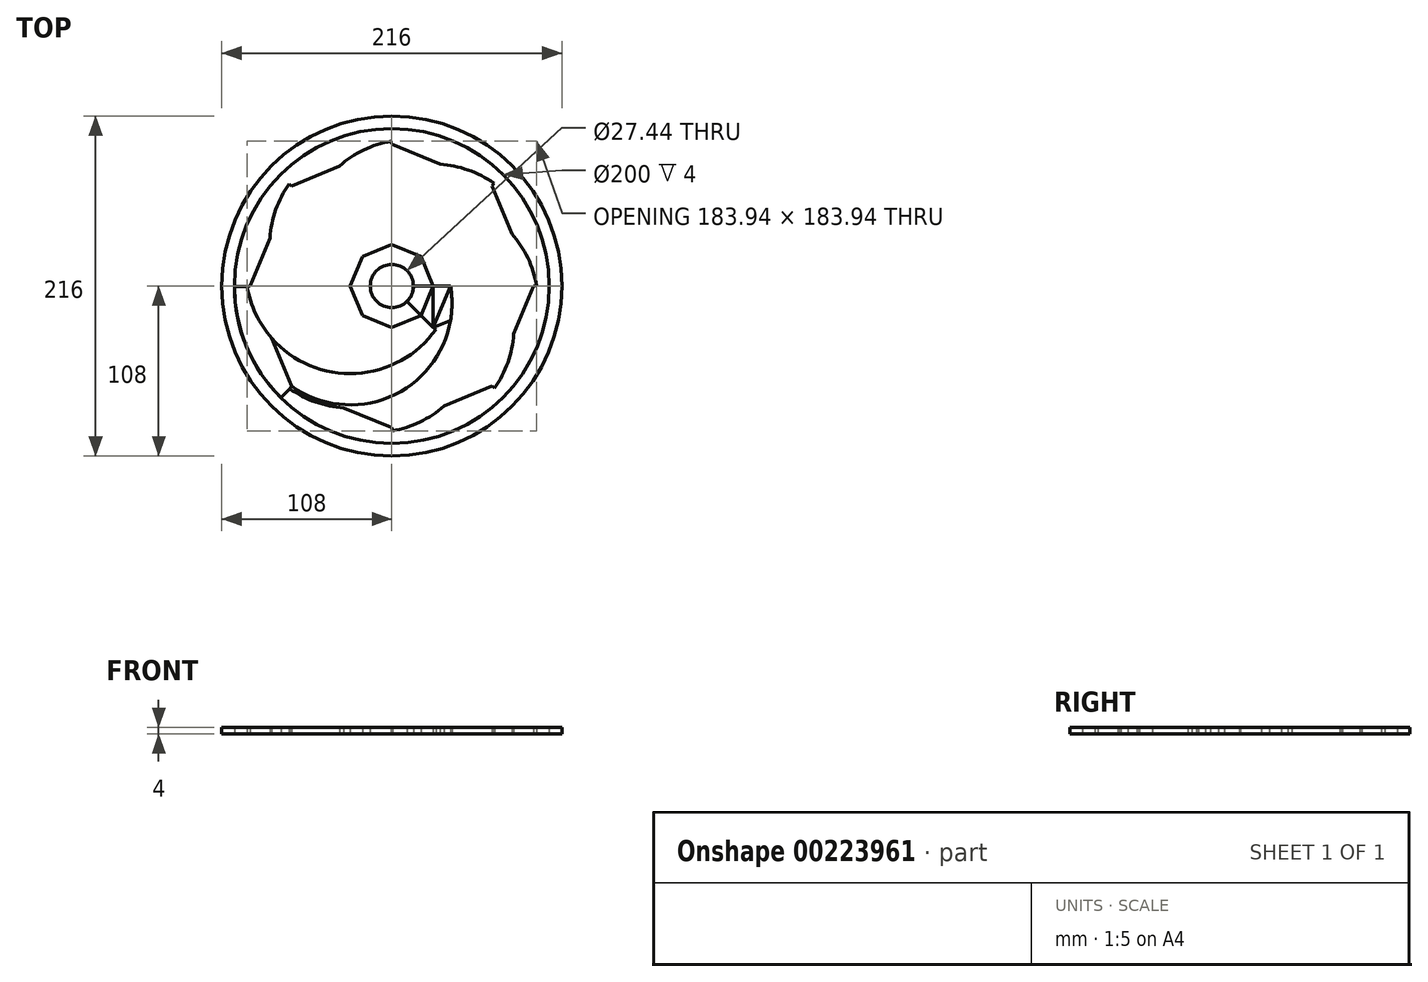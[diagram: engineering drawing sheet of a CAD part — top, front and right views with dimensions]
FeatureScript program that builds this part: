
annotation { "Feature Type Name" : "Feature", "Feature Type Description" : "" }
export const myFeature = defineFeature(function(context is Context, id is Id, definition is map)
    precondition{}
    {
        {
            assignVariable(context, id + "F0", {"name" : "t", "anyValue" : 4});
        }
        {
            var Q0;
            Q0=qCreatedBy(makeId("Top.planeOp"),FACE);
            var sketch = newSketch(context, id + "F1", { "sketchPlane" : qUnion([Q0])});
            skCircle(sketch, "E0", {"center": v(0, 0) * mm, "radius": 100 * mm});
            skCircle(sketch, "E1.cCircle", {"center": v(0, 0) * mm, "radius": 90 * mm, "construction": true});
            skLineSegment(sketch, "E1.0", {"start": v(90, 0) * mm, "end": v(63.64, -63.64) * mm, "construction": true});
            skLineSegment(sketch, "E1.1", {"start": v(63.64, -63.64) * mm, "end": v(0, -90) * mm, "construction": true});
            skLineSegment(sketch, "E1.4", {"start": v(-90, 0) * mm, "end": v(-63.64, 63.64) * mm, "construction": true});
            skLineSegment(sketch, "E1.5", {"start": v(-63.64, 63.64) * mm, "end": v(0, 90) * mm, "construction": true});
            skLineSegment(sketch, "E1.6", {"start": v(0, 90) * mm, "end": v(63.64, 63.64) * mm, "construction": true});
            skLineSegment(sketch, "E1.7", {"start": v(63.64, 63.64) * mm, "end": v(90, 0) * mm, "construction": true});
            skLineSegment(sketch, "E2.0", {"start": v(26.36, -26.36) * mm, "end": v(0, -37.28) * mm});
            skLineSegment(sketch, "E2.1", {"start": v(0, -37.28) * mm, "end": v(-26.36, -26.36) * mm});
            skLineSegment(sketch, "E2.2", {"start": v(-26.36, -26.36) * mm, "end": v(-37.28, 0) * mm});
            skLineSegment(sketch, "E2.3", {"start": v(-37.28, 0) * mm, "end": v(-26.36, 26.36) * mm});
            skLineSegment(sketch, "E2.4", {"start": v(-26.36, 26.36) * mm, "end": v(0, 37.28) * mm});
            skLineSegment(sketch, "E2.5", {"start": v(0, 37.28) * mm, "end": v(26.36, 26.36) * mm});
            skLineSegment(sketch, "E2.6", {"start": v(26.36, 26.36) * mm, "end": v(37.28, 0) * mm});
            skLineSegment(sketch, "E2.7", {"start": v(37.28, 0) * mm, "end": v(26.36, -26.36) * mm});
            skArc(sketch, "E3", {"start": v(-63.64, -63.64) * mm, "mid": v(8.08, -65.54) * mm, "end": v(37.28, 0) * mm});
            skArc(sketch, "E4.0", {"start": v(-64.8, -65.27) * mm, "mid": v(9.15, -67.23) * mm, "end": v(39.25, 0.34) * mm});
            skArc(sketch, "E5.1.0", {"start": v(0, -90) * mm, "mid": v(52.05, -40.63) * mm, "end": v(26.36, 26.36) * mm});
            skArc(sketch, "E5.1.1", {"start": v(0.34, -91.97) * mm, "mid": v(54, -41.07) * mm, "end": v(27.52, 28) * mm});
            skArc(sketch, "E5.2.0", {"start": v(63.64, -63.64) * mm, "mid": v(65.54, 8.08) * mm, "end": v(0, 37.28) * mm});
            skArc(sketch, "E5.2.1", {"start": v(65.27, -64.8) * mm, "mid": v(67.23, 9.15) * mm, "end": v(-0.34, 39.25) * mm});
            skArc(sketch, "E5.3.0", {"start": v(90, 0) * mm, "mid": v(40.63, 52.05) * mm, "end": v(-26.36, 26.36) * mm});
            skArc(sketch, "E5.3.1", {"start": v(91.97, 0.34) * mm, "mid": v(41.07, 54) * mm, "end": v(-28, 27.52) * mm});
            skArc(sketch, "E5.4.0", {"start": v(63.64, 63.64) * mm, "mid": v(-8.08, 65.54) * mm, "end": v(-37.28, 0) * mm});
            skArc(sketch, "E5.4.1", {"start": v(64.8, 65.27) * mm, "mid": v(-9.15, 67.23) * mm, "end": v(-39.25, -0.34) * mm});
            skArc(sketch, "E5.5.0", {"start": v(0, 90) * mm, "mid": v(-52.05, 40.63) * mm, "end": v(-26.36, -26.36) * mm});
            skArc(sketch, "E5.5.1", {"start": v(-0.34, 91.97) * mm, "mid": v(-54, 41.07) * mm, "end": v(-27.52, -28) * mm});
            skArc(sketch, "E5.6.0", {"start": v(-63.64, 63.64) * mm, "mid": v(-65.54, -8.08) * mm, "end": v(0, -37.28) * mm});
            skArc(sketch, "E5.6.1", {"start": v(-65.27, 64.8) * mm, "mid": v(-67.23, -9.15) * mm, "end": v(0.34, -39.25) * mm});
            skArc(sketch, "E5.7.0", {"start": v(-90, 0) * mm, "mid": v(-40.63, -52.05) * mm, "end": v(26.36, -26.36) * mm});
            skArc(sketch, "E5.7.1", {"start": v(-91.97, -0.34) * mm, "mid": v(-41.07, -54) * mm, "end": v(28, -27.52) * mm});
            skLineSegment(sketch, "E6", {"start": v(37.28, -21.84) * mm, "end": v(26.36, -26.36) * mm});
            skLineSegment(sketch, "E7", {"start": v(28, -27.52) * mm, "end": v(26.36, -26.36) * mm});
            skLineSegment(sketch, "E8", {"start": v(-64.8, -65.27) * mm, "end": v(-63.64, -63.64) * mm});
            skLineSegment(sketch, "E9", {"start": v(-63.64, -63.64) * mm, "end": v(-76.28, -33.12) * mm});
            skLineSegment(sketch, "E10.1.0", {"start": v(0, -90) * mm, "end": v(-30.52, -77.36) * mm});
            skLineSegment(sketch, "E10.1.1", {"start": v(0.34, -91.97) * mm, "end": v(0, -90) * mm});
            skLineSegment(sketch, "E10.1.2", {"start": v(39.25, 0.34) * mm, "end": v(37.28, 0) * mm});
            skLineSegment(sketch, "E10.2.0", {"start": v(63.64, -63.64) * mm, "end": v(33.12, -76.28) * mm});
            skLineSegment(sketch, "E10.2.1", {"start": v(65.27, -64.8) * mm, "end": v(63.64, -63.64) * mm});
            skLineSegment(sketch, "E10.2.2", {"start": v(27.52, 28) * mm, "end": v(26.36, 26.36) * mm});
            skLineSegment(sketch, "E10.3.0", {"start": v(90, 0) * mm, "end": v(77.36, -30.52) * mm});
            skLineSegment(sketch, "E10.3.1", {"start": v(91.97, 0.34) * mm, "end": v(90, 0) * mm});
            skLineSegment(sketch, "E10.3.2", {"start": v(-0.34, 39.25) * mm, "end": v(0, 37.28) * mm});
            skLineSegment(sketch, "E10.4.0", {"start": v(63.64, 63.64) * mm, "end": v(76.28, 33.12) * mm});
            skLineSegment(sketch, "E10.4.1", {"start": v(64.8, 65.27) * mm, "end": v(63.64, 63.64) * mm});
            skLineSegment(sketch, "E10.4.2", {"start": v(-28, 27.52) * mm, "end": v(-26.36, 26.36) * mm});
            skLineSegment(sketch, "E10.5.0", {"start": v(0, 90) * mm, "end": v(30.52, 77.36) * mm});
            skLineSegment(sketch, "E10.5.1", {"start": v(-0.34, 91.97) * mm, "end": v(0, 90) * mm});
            skLineSegment(sketch, "E10.5.2", {"start": v(-39.25, -0.34) * mm, "end": v(-37.28, 0) * mm});
            skLineSegment(sketch, "E10.6.0", {"start": v(-63.64, 63.64) * mm, "end": v(-33.12, 76.28) * mm});
            skLineSegment(sketch, "E10.6.1", {"start": v(-65.27, 64.8) * mm, "end": v(-63.64, 63.64) * mm});
            skLineSegment(sketch, "E10.6.2", {"start": v(-27.52, -28) * mm, "end": v(-26.36, -26.36) * mm});
            skLineSegment(sketch, "E10.7.0", {"start": v(-90, 0) * mm, "end": v(-77.36, 30.52) * mm});
            skLineSegment(sketch, "E10.7.1", {"start": v(-91.97, -0.34) * mm, "end": v(-90, 0) * mm});
            skLineSegment(sketch, "E10.7.2", {"start": v(0.34, -39.25) * mm, "end": v(0, -37.28) * mm});
            skLineSegment(sketch, "E11.1.0", {"start": v(41.8, 10.92) * mm, "end": v(37.28, 0) * mm});
            skLineSegment(sketch, "E11.2.0", {"start": v(21.84, 37.28) * mm, "end": v(26.36, 26.36) * mm});
            skLineSegment(sketch, "E11.3.0", {"start": v(-10.92, 41.8) * mm, "end": v(0, 37.28) * mm});
            skLineSegment(sketch, "E11.4.0", {"start": v(-37.28, 21.84) * mm, "end": v(-26.36, 26.36) * mm});
            skLineSegment(sketch, "E11.5.0", {"start": v(-41.8, -10.92) * mm, "end": v(-37.28, 0) * mm});
            skLineSegment(sketch, "E11.6.0", {"start": v(-21.84, -37.28) * mm, "end": v(-26.36, -26.36) * mm});
            skLineSegment(sketch, "E11.7.0", {"start": v(10.92, -41.8) * mm, "end": v(0, -37.28) * mm});
            skLineSegment(sketch, "E12", {"start": v(18.64, -18.64) * mm, "end": v(0, -26.36) * mm});
            skPoint(sketch, "E13", {"position": v(18.64, -18.64) * mm});
            skLineSegment(sketch, "E14", {"start": v(18.64, -18.64) * mm, "end": v(0, -37.28) * mm});
            skLineSegment(sketch, "E15", {"start": v(0, -26.36) * mm, "end": v(0, -37.28) * mm});
            skLineSegment(sketch, "E16.1.0", {"start": v(26.36, 0) * mm, "end": v(18.64, -18.64) * mm});
            skLineSegment(sketch, "E16.1.1", {"start": v(18.64, -18.64) * mm, "end": v(26.36, -26.36) * mm});
            skLineSegment(sketch, "E16.1.2", {"start": v(26.36, 0) * mm, "end": v(26.36, -26.36) * mm});
            skLineSegment(sketch, "E16.2.0", {"start": v(18.64, 18.64) * mm, "end": v(26.36, 0) * mm});
            skLineSegment(sketch, "E16.2.1", {"start": v(26.36, 0) * mm, "end": v(37.28, 0) * mm});
            skLineSegment(sketch, "E16.2.2", {"start": v(18.64, 18.64) * mm, "end": v(37.28, 0) * mm});
            skLineSegment(sketch, "E17.3.3.0", {"start": v(18.64, 18.64) * mm, "end": v(26.36, 26.36) * mm});
            skLineSegment(sketch, "E17.5.3.0", {"start": v(0, 26.36) * mm, "end": v(18.64, 18.64) * mm});
            skLineSegment(sketch, "E17.6.3.0", {"start": v(0, 26.36) * mm, "end": v(26.36, 26.36) * mm});
            skLineSegment(sketch, "E17.3.4.0", {"start": v(0, 26.36) * mm, "end": v(0, 37.28) * mm});
            skLineSegment(sketch, "E17.5.4.0", {"start": v(-18.64, 18.64) * mm, "end": v(0, 26.36) * mm});
            skLineSegment(sketch, "E17.6.4.0", {"start": v(-18.64, 18.64) * mm, "end": v(0, 37.28) * mm});
            skLineSegment(sketch, "E17.3.5.0", {"start": v(-18.64, 18.64) * mm, "end": v(-26.36, 26.36) * mm});
            skLineSegment(sketch, "E17.5.5.0", {"start": v(-26.36, 0) * mm, "end": v(-18.64, 18.64) * mm});
            skLineSegment(sketch, "E17.6.5.0", {"start": v(-26.36, 0) * mm, "end": v(-26.36, 26.36) * mm});
            skLineSegment(sketch, "E17.3.6.0", {"start": v(-26.36, 0) * mm, "end": v(-37.28, 0) * mm});
            skLineSegment(sketch, "E17.5.6.0", {"start": v(-18.64, -18.64) * mm, "end": v(-26.36, 0) * mm});
            skLineSegment(sketch, "E17.6.6.0", {"start": v(-18.64, -18.64) * mm, "end": v(-37.28, 0) * mm});
            skLineSegment(sketch, "E17.3.7.0", {"start": v(-18.64, -18.64) * mm, "end": v(-26.36, -26.36) * mm});
            skLineSegment(sketch, "E17.5.7.0", {"start": v(0, -26.36) * mm, "end": v(-18.64, -18.64) * mm});
            skLineSegment(sketch, "E17.6.7.0", {"start": v(0, -26.36) * mm, "end": v(-26.36, -26.36) * mm});
            skLineSegment(sketch, "E18", {"start": v(-91.97, -0.34) * mm, "end": v(-100, -0.34) * mm});
            skLineSegment(sketch, "E19.1.0", {"start": v(-64.8, -65.27) * mm, "end": v(-70.47, -70.95) * mm});
            skLineSegment(sketch, "E19.2.0", {"start": v(0.34, -91.97) * mm, "end": v(0.34, -100) * mm});
            skLineSegment(sketch, "E19.3.0", {"start": v(65.27, -64.8) * mm, "end": v(70.95, -70.47) * mm});
            skLineSegment(sketch, "E19.4.0", {"start": v(91.97, 0.34) * mm, "end": v(100, 0.34) * mm});
            skLineSegment(sketch, "E19.5.0", {"start": v(64.8, 65.27) * mm, "end": v(70.47, 70.95) * mm});
            skLineSegment(sketch, "E19.6.0", {"start": v(-0.34, 91.97) * mm, "end": v(-0.34, 100) * mm});
            skLineSegment(sketch, "E19.7.0", {"start": v(-65.27, 64.8) * mm, "end": v(-70.95, 70.47) * mm});
            skCircle(sketch, "E20", {"center": v(0, 0) * mm, "radius": 13.72 * mm});
            skLineSegment(sketch, "E21", {"start": v(0, 0) * mm, "end": v(18.64, -18.64) * mm});
            skLineSegment(sketch, "E22", {"start": v(0, 0) * mm, "end": v(26.36, 0) * mm});
            skCircle(sketch, "E23.0", {"center": v(0, 0) * mm, "radius": 108 * mm});
            skSolve(sketch);
        }
        {
            var Q0;
            Q0=makeQuery(id+"F1.imprint","IMPRINT",FACE,{"disambiguationData":[TD([[makeQuery(id+"F1.imprint","IMPRINT",EDGE,{"derivedFrom":sQuery(id+"F1.wireOp",EDGE,"E0")}),1.0]])]});
            extrude(context, id + "F2", {"entities" : qUnion([Q0]), "depth" : (getVariable(context, 't')) * mm});
        }
        {
            var Q0;
            {var subQ1=sQuery(id+"F1.wireOp",EDGE,"E6");Q0=makeQuery(id+"F1.imprint","IMPRINT",FACE,{"disambiguationData":[TD([[makeQuery(id+"F1.imprint","IMPRINT",EDGE,{"derivedFrom":subQ1}),1.0]])]});}
            extrude(context, id + "F3", {"entities" : qUnion([Q0]), "depth" : (getVariable(context, 't')) * mm});
        }
        {
            var Q0;
            {var subQ0=sQuery(id+"F1.wireOp",EDGE,"E2.7");Q0=makeQuery(id+"F1.imprint","IMPRINT",FACE,{"disambiguationData":[TD([[makeQuery(id+"F1.imprint","IMPRINT",EDGE,{"derivedFrom":subQ0}),1.0]])]});}
            extrude(context, id + "F4", {"entities" : qUnion([Q0]), "depth" : (getVariable(context, 't')) * mm});
        }
        {
            var Q0;
            Q0=makeQuery(id+"F1.imprint","IMPRINT",FACE,{"disambiguationData":[TD([[makeQuery(id+"F1.imprint","IMPRINT",EDGE,{"derivedFrom":sQuery(id+"F1.wireOp",EDGE,"E2.7")}),-1.0]])]});
            extrude(context, id + "F5", {"entities" : qUnion([Q0]), "depth" : (getVariable(context, 't')) * mm});
        }
        {
            var Q0;
            Q0=makeQuery(id+"F1.imprint","IMPRINT",FACE,{"disambiguationData":[TD([[makeQuery(id+"F1.imprint","IMPRINT",EDGE,{"derivedFrom":sQuery(id+"F1.wireOp",EDGE,"E16.1.0")}),1.0]])]});
            extrude(context, id + "F6", {"entities" : qUnion([Q0]), "depth" : (getVariable(context, 't')) * mm});
        }
        {
            var Q0;
            Q0=makeQuery(id+"F1.imprint","IMPRINT",FACE,{"disambiguationData":[TD([[makeQuery(id+"F1.imprint","IMPRINT",EDGE,{"derivedFrom":sQuery(id+"F1.wireOp",EDGE,"E12")}),-1.0]])]});
            var Q1;
            {var subQ0=sQuery(id+"F1.wireOp",EDGE,"E16.1.0");Q1=makeQuery(id+"F1.imprint","IMPRINT",FACE,{"disambiguationData":[TD([[makeQuery(id+"F1.imprint","IMPRINT",EDGE,{"derivedFrom":subQ0}),-1.0]])]});}
            extrude(context, id + "F7", {"entities" : qUnion([Q0, Q1]), "depth" : (getVariable(context, 't')) * mm});
        }
        {
            var Q0;
            Q0=makeQuery(id+"F1.imprint","IMPRINT",FACE,{"disambiguationData":[TD([[makeQuery(id+"F1.imprint","IMPRINT",EDGE,{"derivedFrom":sQuery(id+"F1.wireOp",EDGE,"E8")}),1.0]])]});
            extrude(context, id + "F8", {"entities" : qUnion([Q0]), "depth" : (getVariable(context, 't')) * mm});
        }
        {
            var Q0;
            {var subQ0=sQuery(id+"F1.wireOp",EDGE,"E16.1.0");Q0=makeQuery(id+"F1.imprint","IMPRINT",FACE,{"disambiguationData":[TD([[makeQuery(id+"F1.imprint","IMPRINT",EDGE,{"derivedFrom":subQ0}),-1.0]])]});}
            extrude(context, id + "F9", {"entities" : qUnion([Q0]), "depth" : (getVariable(context, 't')) * mm});
        }
        {
            var Q0;
            Q0 = qSketchRegion(id + "F1", true);
            extrude(context, id + "F10", {"entities" : qUnion([Q0]), "depth" : (getVariable(context, 't')) * mm});
        }
    });
